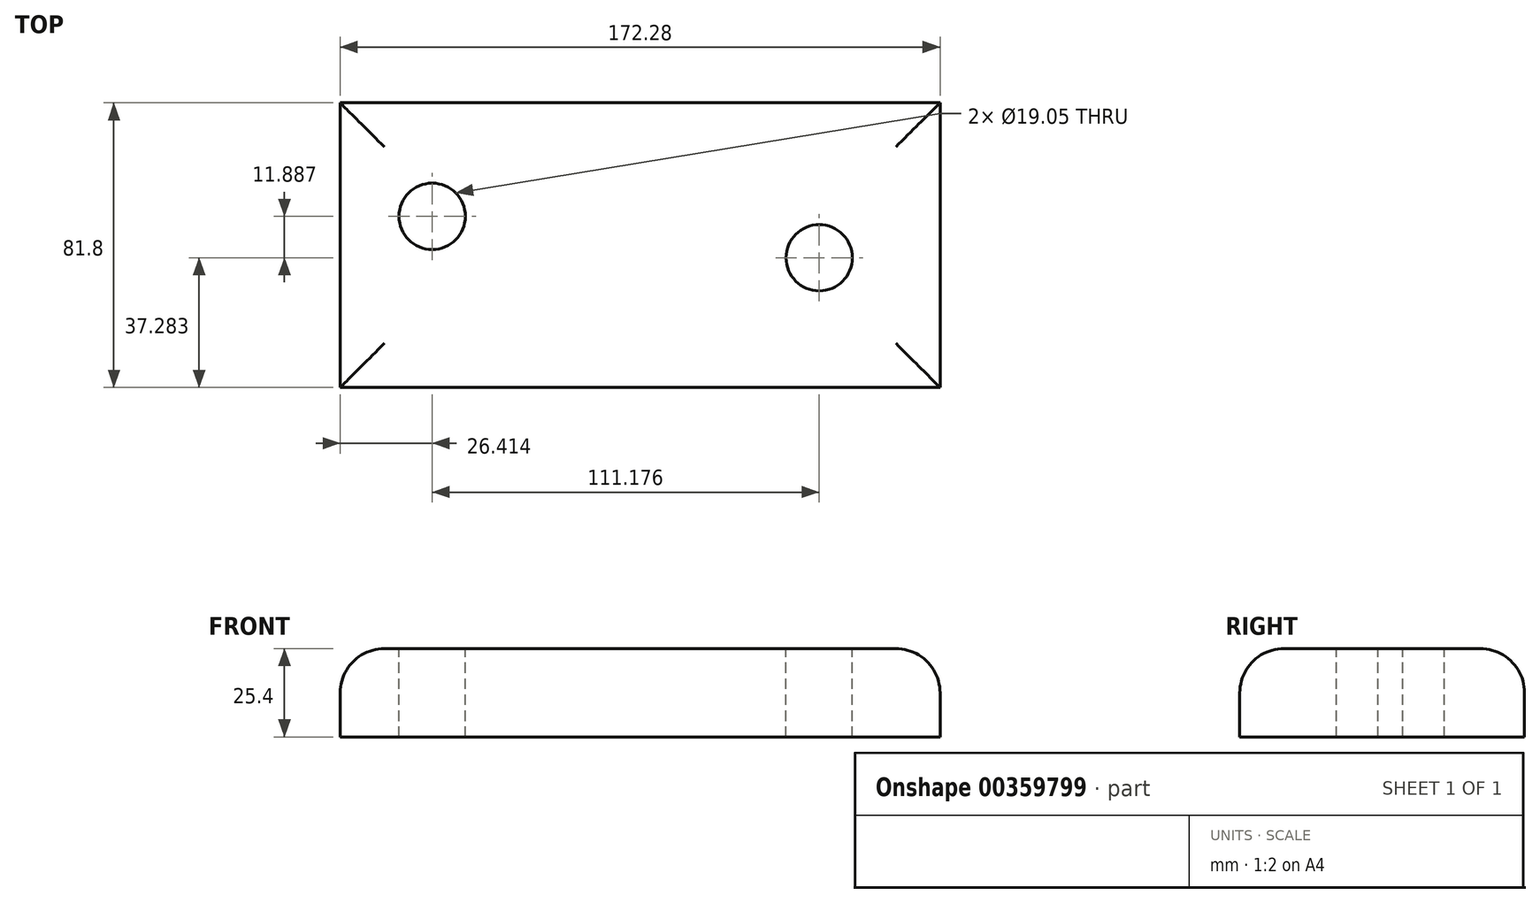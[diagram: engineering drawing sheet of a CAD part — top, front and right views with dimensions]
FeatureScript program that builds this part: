
annotation { "Feature Type Name" : "Feature", "Feature Type Description" : "" }
export const myFeature = defineFeature(function(context is Context, id is Id, definition is map)
    precondition{}
    {
        {
            var Q0;
            Q0=qCreatedBy(makeId("Top.planeOp"),FACE);
            var sketch = newSketch(context, id + "F0", { "sketchPlane" : qUnion([Q0])});
            skLineSegment(sketch, "E0.bottom", {"start": v(86.14, 0) * mm, "end": v(-86.14, 0) * mm});
            skLineSegment(sketch, "E0.top", {"start": v(86.14, 81.8) * mm, "end": v(-86.14, 81.8) * mm});
            skLineSegment(sketch, "E0.left", {"start": v(86.14, 0) * mm, "end": v(86.14, 81.8) * mm});
            skLineSegment(sketch, "E0.right", {"start": v(-86.14, 0) * mm, "end": v(-86.14, 81.8) * mm});
            skPoint(sketch, "E0.middle", {"position": v(0, 40.9) * mm});
            skSolve(sketch);
        }
        {
            var Q0;
            Q0=makeQuery(id+"F0.imprint","IMPRINT",FACE,{"disambiguationData":[TD([[makeQuery(id+"F0.imprint","IMPRINT",EDGE,{"derivedFrom":sQuery(id+"F0.wireOp",EDGE,"E0.bottom")}),-1.0]])]});
            extrude(context, id + "F1", {"entities" : qUnion([Q0]), "depth" : 25.4 * mm});
        }
        {
            var Q0;
            Q0=makeQuery(id+"F1.opExtrude","CAP_FACE",FACE,{"disambiguationData":[OSD([sQuery(id+"F0.wireOp",EDGE,"E0.bottom"),sQuery(id+"F0.wireOp",EDGE,"E0.top"),sQuery(id+"F0.wireOp",EDGE,"E0.left"),sQuery(id+"F0.wireOp",EDGE,"E0.right")])],"isStart":false});
            var sketch = newSketch(context, id + "F2", { "sketchPlane" : qUnion([Q0])});
            skPoint(sketch, "E1", {"position": v(-59.73, 49.17) * mm});
            skPoint(sketch, "E2", {"position": v(51.45, 37.28) * mm});
            skSolve(sketch);
        }
        {
            var Q0;
            Q0=sQuery(id+"F2.wireOp",VERTEX,"E2");
            var Q1;
            Q1=sQuery(id+"F2.wireOp",VERTEX,"E1");
            var Q2;
            Q2=makeQuery(id+"F1.opExtrude","SWEPT_BODY",BODY,{"disambiguationData":[OSD([sQuery(id+"F0.wireOp",EDGE,"E0.bottom"),sQuery(id+"F0.wireOp",EDGE,"E0.top"),sQuery(id+"F0.wireOp",EDGE,"E0.left"),sQuery(id+"F0.wireOp",EDGE,"E0.right")])]});
            hole(context, id + "F3", {"style" : HoleStyle.SIMPLE, "endStyle" : HoleEndStyle.THROUGH, "holeDiameter" : 19.05 * mm, "isTappedThrough" : true, "tappedDepth" : 12.7 * mm, "tapClearance" : 3, "locations" : qUnion([Q0, Q1]), "scope" : qUnion([Q2])});
        }
        {
            var Q0;
            Q0=makeQuery(id+"F1.opExtrude","CAP_EDGE",EDGE,{"disambiguationData":[OSD([sQuery(id+"F0.wireOp",EDGE,"E0.top")])],"isStart":false});
            var Q1;
            Q1=makeQuery(id+"F1.opExtrude","CAP_EDGE",EDGE,{"disambiguationData":[OSD([sQuery(id+"F0.wireOp",EDGE,"E0.right")])],"isStart":false});
            var Q2;
            Q2=makeQuery(id+"F1.opExtrude","CAP_EDGE",EDGE,{"disambiguationData":[OSD([sQuery(id+"F0.wireOp",EDGE,"E0.bottom")])],"isStart":false});
            var Q3;
            Q3=makeQuery(id+"F1.opExtrude","CAP_EDGE",EDGE,{"disambiguationData":[OSD([sQuery(id+"F0.wireOp",EDGE,"E0.left")])],"isStart":false});
            fillet(context, id + "F4", {"entities" : qUnion([Q0, Q1, Q2, Q3]), "radius" : 12.7 * mm, "tangentPropagation" : true, "allowEdgeOverflow" : false});
        }
    });
